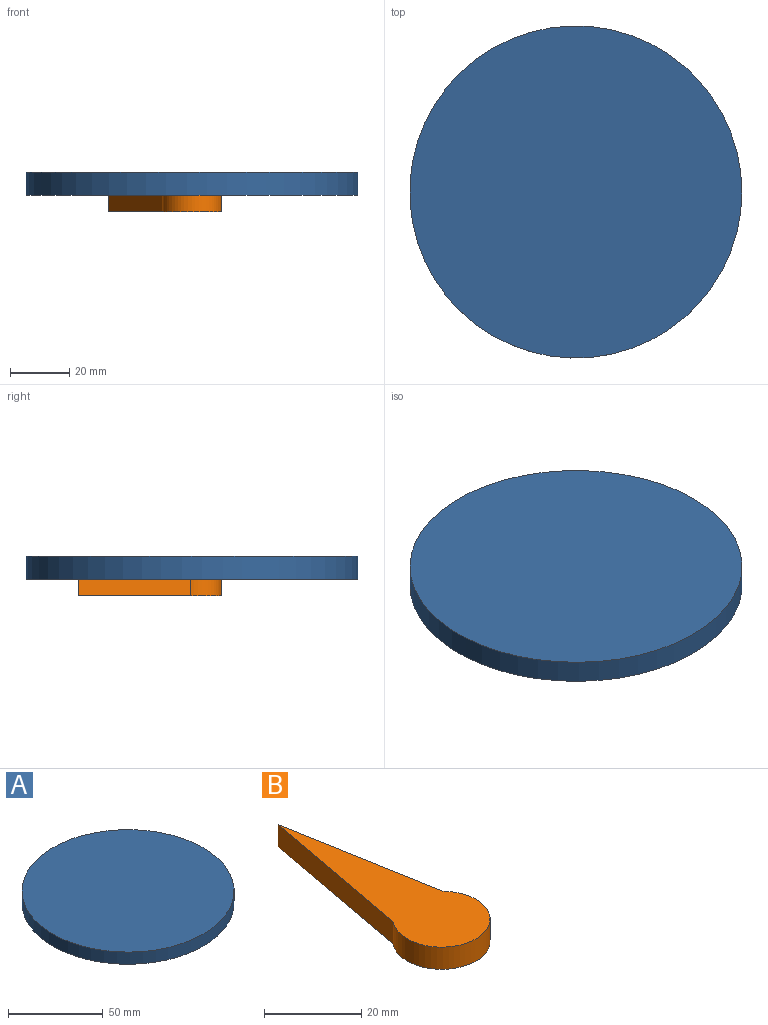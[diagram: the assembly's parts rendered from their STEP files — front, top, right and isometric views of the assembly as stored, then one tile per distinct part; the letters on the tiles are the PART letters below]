
ASSEMBLY  parts=2 mates=1
PART A: 3 faces, bbox 112.2x112.2x7.9 mm
  f0: cylinder r=56.09mm len=112.18mm, axis (0,0,-1), area 2775mm2, adj f1,f2
  f1: plane 112.18x112.18mm, normal (0,0,1), area 9883.7mm2, adj f0
  f2: plane 112.18x112.18mm, normal (0,0,-1), area 9883.7mm2, adj f0
PART B: 5 faces, bbox 20x57.5x5.6 mm
  f0: plane 41.3x7.77mm, normal (-0.98,0.18,0), area 234.8mm2, adj f1,f2,f3,f4
  f1: cylinder r=9.98mm len=19.95mm, axis (0,0,1), area 255.2mm2, adj f0,f2,f3,f4
  f2: plane 40.7x7.24mm, normal (0.98,0.18,0), area 231mm2, adj f0,f1,f3,f4
  f3: plane 57.54x19.95mm, normal (0,0,-1), area 584.8mm2, adj f0,f1,f2
  f4: plane 57.54x19.95mm, normal (0,0,1), area 584.8mm2, adj f0,f1,f2
PLACE A t=(-0.66,-2.94,-5.4)mm fixed
PLACE B rot(axis=(0,0,1),36.5deg) t=(-0.66,-2.94,-5.4)mm
MATE revolute A.f0 <-> B.f1  axis (0,0,-1) through (-0.66,-2.94,-5.4)mm
